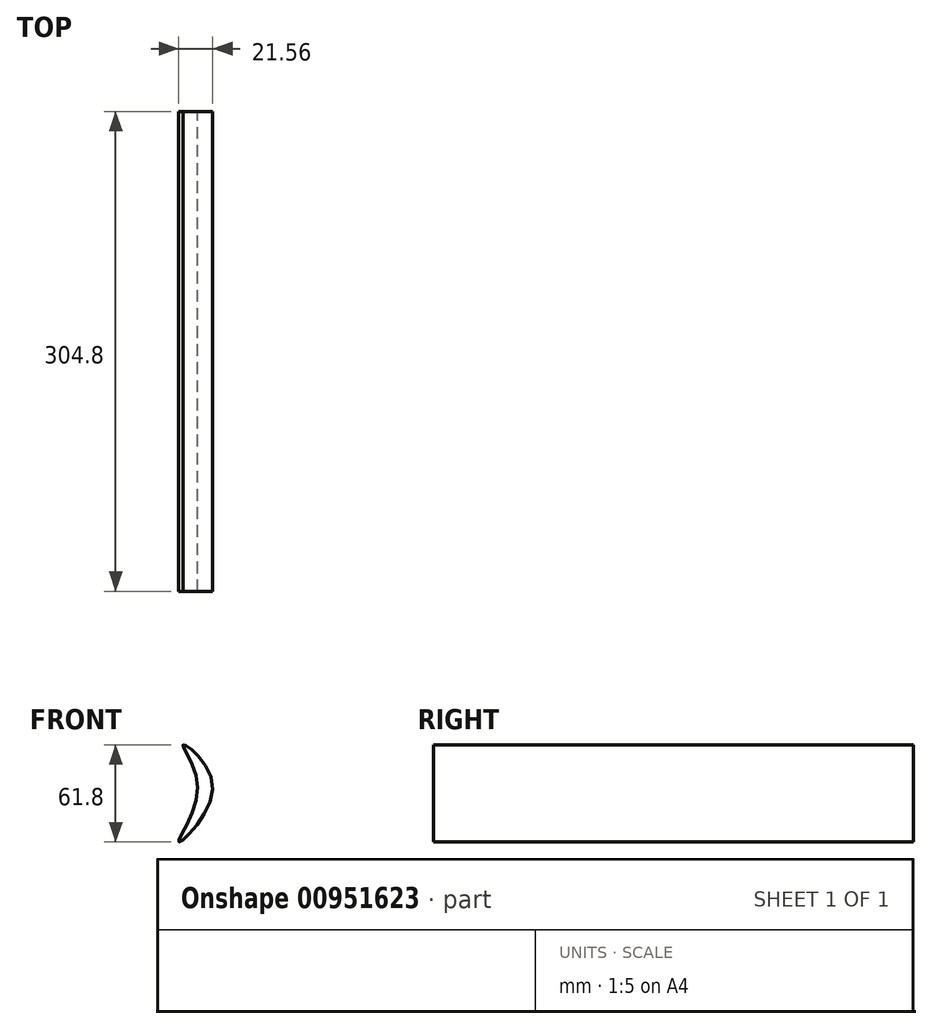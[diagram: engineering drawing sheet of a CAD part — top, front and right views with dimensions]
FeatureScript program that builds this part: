
annotation { "Feature Type Name" : "Feature", "Feature Type Description" : "" }
export const myFeature = defineFeature(function(context is Context, id is Id, definition is map)
    precondition{}
    {
        {
            var Q0;
            Q0=qCreatedBy(makeId("Front.planeOp"),FACE);
            var sketch = newSketch(context, id + "F0", { "sketchPlane" : qUnion([Q0])});
            skFitSpline(sketch, "E0", {"points": [v(-36.18, 7.35) * mm, v(-45.25, 34.47) * mm, v(-26.6, 7.87) * mm, v(-47.97, -27.28) * mm, v(-36.18, 7.35) * mm]});
            skSolve(sketch);
        }
        {
            var Q0;
            Q0=makeQuery(id+"F0.imprint","IMPRINT",FACE,{"disambiguationData":[TD([[makeQuery(id+"F0.imprint","IMPRINT",EDGE,{"derivedFrom":sQuery(id+"F0.wireOp",EDGE,"E0")}),-1.0]])]});
            extrude(context, id + "F1", {"entities" : qUnion([Q0]), "depth" : 304.8 * mm, "offsetDistance" : 25.4 * mm});
        }
    });
